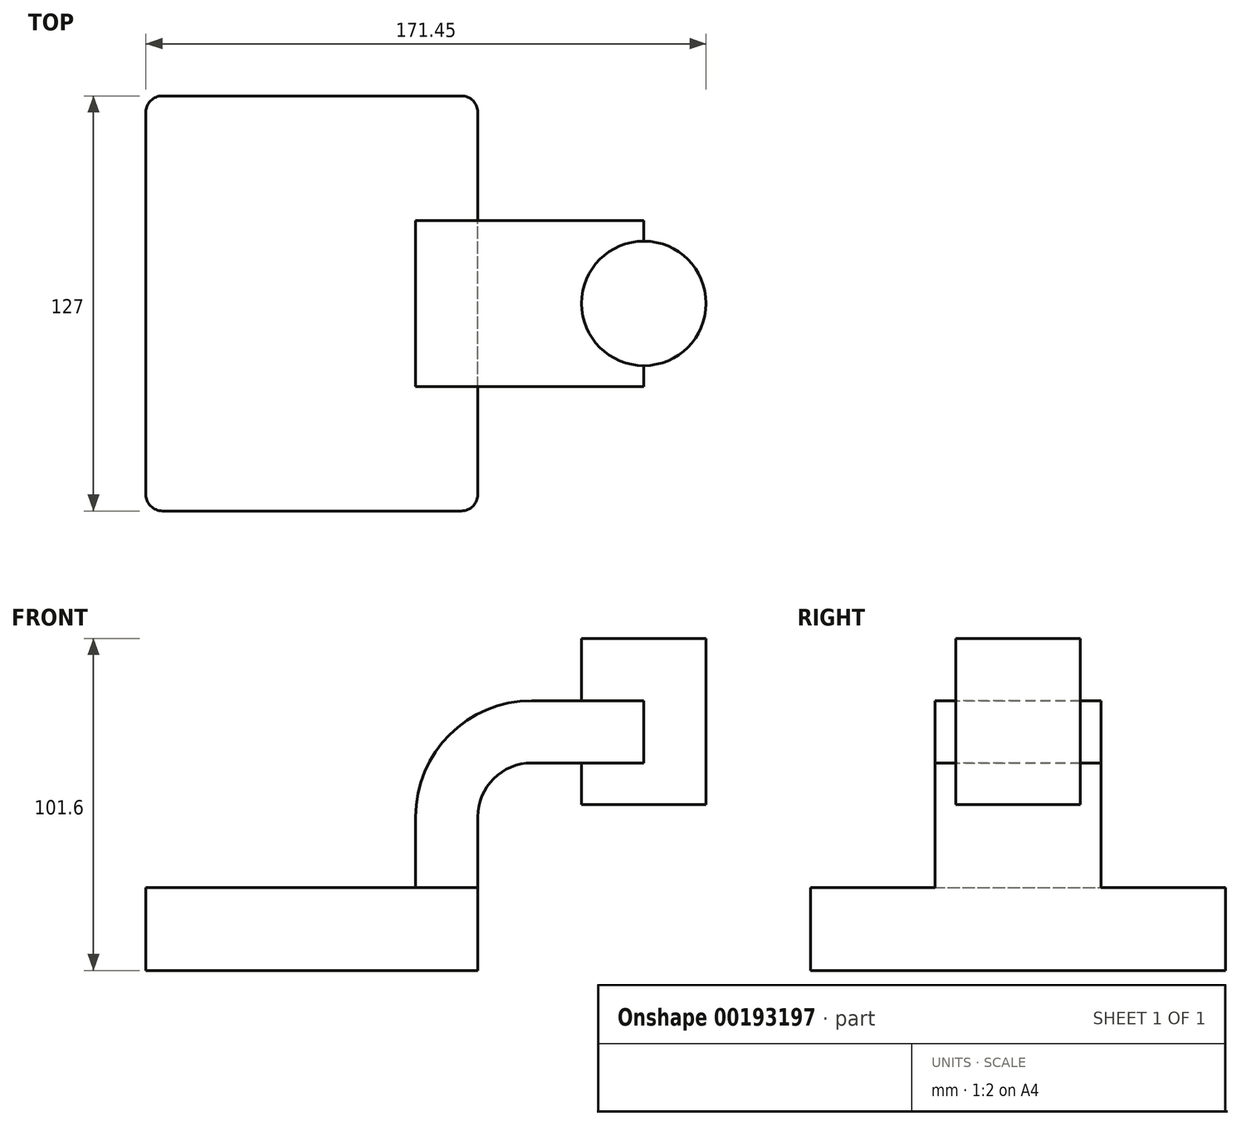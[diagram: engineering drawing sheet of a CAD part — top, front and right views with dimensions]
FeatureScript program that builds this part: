
annotation { "Feature Type Name" : "Feature", "Feature Type Description" : "" }
export const myFeature = defineFeature(function(context is Context, id is Id, definition is map)
    precondition{}
    {
        {
            var Q0;
            Q0=qCreatedBy(makeId("Front.planeOp"),FACE);
            var sketch = newSketch(context, id + "F0", { "sketchPlane" : qUnion([Q0])});
            skLineSegment(sketch, "E0.bottom", {"start": v(-50.8, -12.7) * mm, "end": v(50.8, -12.7) * mm});
            skLineSegment(sketch, "E0.top", {"start": v(-50.8, 12.7) * mm, "end": v(50.8, 12.7) * mm});
            skLineSegment(sketch, "E0.left", {"start": v(-50.8, -12.7) * mm, "end": v(-50.8, 12.7) * mm});
            skLineSegment(sketch, "E0.right", {"start": v(50.8, -12.7) * mm, "end": v(50.8, 12.7) * mm});
            skPoint(sketch, "E0.middle", {"position": v(0, 0) * mm});
            skLineSegment(sketch, "E1.bottom", {"start": v(120.65, 38.1) * mm, "end": v(82.55, 38.1) * mm});
            skLineSegment(sketch, "E1.top", {"start": v(120.65, 88.9) * mm, "end": v(82.55, 88.9) * mm});
            skLineSegment(sketch, "E1.left", {"start": v(120.65, 38.1) * mm, "end": v(120.65, 88.9) * mm});
            skLineSegment(sketch, "E1.right", {"start": v(82.55, 38.1) * mm, "end": v(82.55, 88.9) * mm});
            skPoint(sketch, "E1.middle", {"position": v(101.6, 63.5) * mm});
            skLineSegment(sketch, "E2", {"start": v(50.8, 12.7) * mm, "end": v(50.8, 34.3) * mm});
            skArc(sketch, "E3", {"start": v(50.8, 34.3) * mm, "mid": v(55.64, 45.96) * mm, "end": v(67.3, 50.8) * mm});
            skLineSegment(sketch, "E4", {"start": v(67.3, 50.8) * mm, "end": v(101.6, 50.8) * mm});
            skLineSegment(sketch, "E5.0", {"start": v(67.3, 69.85) * mm, "end": v(101.6, 69.85) * mm});
            skArc(sketch, "E5.1", {"start": v(31.75, 34.3) * mm, "mid": v(42.17, 59.43) * mm, "end": v(67.3, 69.85) * mm});
            skLineSegment(sketch, "E5.2", {"start": v(31.75, 12.7) * mm, "end": v(31.75, 34.3) * mm});
            skFitSpline(sketch, "E6", {"points": [v(-50.8, 12.7) * mm, v(67.31, 69.85) * mm], "startDerivative": vector(69.1, 104.16) * mm, "endDerivative": vector(143.46, -30.67) * mm});
            skLineSegment(sketch, "E7", {"start": v(101.6, 38.1) * mm, "end": v(101.6, 88.9) * mm});
            skSolve(sketch);
        }
        {
            var Q0;
            Q0=makeQuery(id+"F0.imprint","IMPRINT",FACE,{"disambiguationData":[TD([[makeQuery(id+"F0.imprint","IMPRINT",EDGE,{"derivedFrom":sQuery(id+"F0.wireOp",EDGE,"E0.bottom")}),1.0]])]});
            extrude(context, id + "F1", {"entities" : qUnion([Q0]), "endBound" : BoundingType.SYMMETRIC, "depth" : 127 * mm});
        }
        {
            var Q0;
            {var subQ0=sQuery(id+"F0.wireOp",EDGE,"E4");var subQ1=sQuery(id+"F0.wireOp",EDGE,"E1.right");var subQ2=makeQuery(id+"F0.imprint","INTERSECT",VERTEX,{"derivedFrom":[subQ1,subQ0]});Q0=makeQuery(id+"F0.imprint","IMPRINT",FACE,{"disambiguationData":[TD([[makeQuery(id+"F0.imprint","IMPRINT",EDGE,{"disambiguationData":[TD([[subQ2,-1.0]])],"derivedFrom":subQ1}),-1.0]])]});}
            var Q1;
            {var subQ1=sQuery(id+"F0.wireOp",EDGE,"E2");Q1=makeQuery(id+"F0.imprint","IMPRINT",FACE,{"disambiguationData":[TD([[makeQuery(id+"F0.imprint","IMPRINT",EDGE,{"derivedFrom":subQ1}),1.0]])]});}
            extrude(context, id + "F2", {"entities" : qUnion([Q0, Q1]), "operationType" : NewBodyOperationType.ADD, "endBound" : BoundingType.SYMMETRIC, "depth" : 50.8 * mm});
        }
        {
            var Q0;
            Q0=makeQuery(id+"F0.imprint","IMPRINT",FACE,{"disambiguationData":[TD([[makeQuery(id+"F0.imprint","IMPRINT",EDGE,{"derivedFrom":sQuery(id+"F0.wireOp",EDGE,"E5.1")}),1.0]])]});
            extrude(context, id + "F3", {"entities" : qUnion([Q0]), "operationType" : NewBodyOperationType.ADD, "endBound" : BoundingType.SYMMETRIC, "depth" : 15.88 * mm});
        }
        {
            var Q0;
            {var subQ0=sQuery(id+"F0.wireOp",EDGE,"E1.left");Q0=makeQuery(id+"F0.imprint","IMPRINT",FACE,{"disambiguationData":[TD([[makeQuery(id+"F0.imprint","IMPRINT",EDGE,{"derivedFrom":subQ0}),1.0]])]});}
            var Q1;
            Q1=sQuery(id+"F0.wireOp",EDGE,"E7");
            revolve(context, id + "F4", {"operationType" : NewBodyOperationType.ADD, "entities" : qUnion([Q0]), "axis" : qUnion([Q1]), "revolveType" : RevolveType.FULL});
        }
        {
            var Q0;
            Q0=makeQuery(id+"F1.opExtrude","CAP_EDGE",EDGE,{"disambiguationData":[OSD([sQuery(id+"F0.wireOp",EDGE,"E0.left")])],"isStart":false});
            var Q1;
            Q1=makeQuery(id+"F1.opExtrude","CAP_EDGE",EDGE,{"disambiguationData":[OSD([sQuery(id+"F0.wireOp",EDGE,"E0.right")])],"isStart":false});
            var Q2;
            Q2=makeQuery(id+"F1.opExtrude","CAP_EDGE",EDGE,{"disambiguationData":[OSD([sQuery(id+"F0.wireOp",EDGE,"E0.right")])],"isStart":true});
            var Q3;
            Q3=makeQuery(id+"F1.opExtrude","CAP_EDGE",EDGE,{"disambiguationData":[OSD([sQuery(id+"F0.wireOp",EDGE,"E0.left")])],"isStart":true});
            fillet(context, id + "F5", {"entities" : qUnion([Q0, Q1, Q2, Q3]), "radius" : 5.08 * mm, "tangentPropagation" : true, "allowEdgeOverflow" : false});
        }
    });
